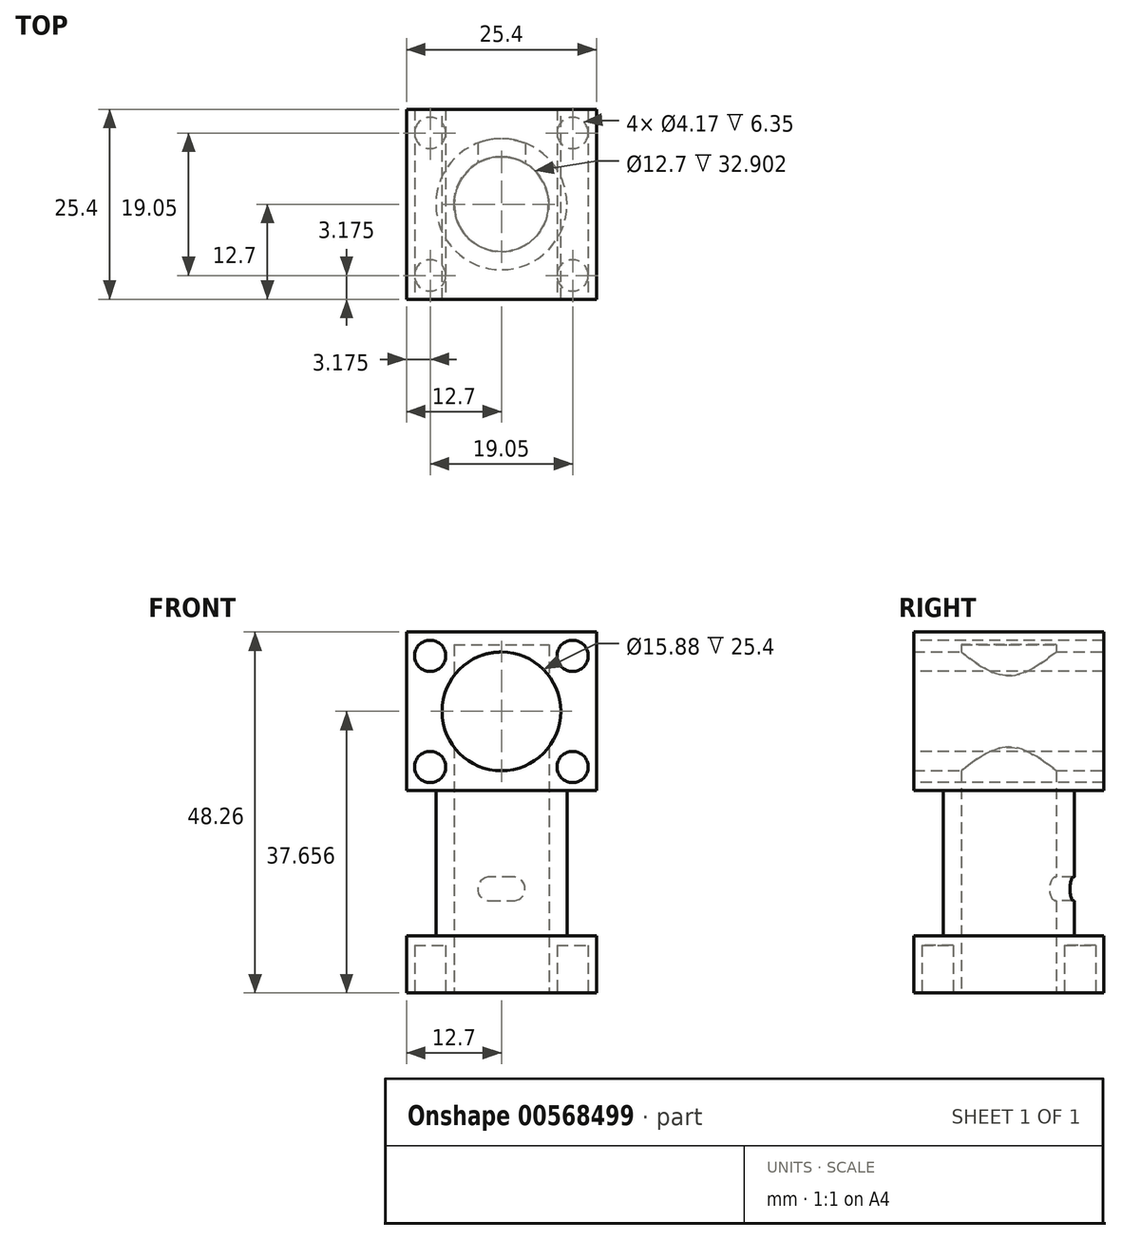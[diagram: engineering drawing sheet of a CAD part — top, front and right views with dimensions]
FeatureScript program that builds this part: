
annotation { "Feature Type Name" : "Feature", "Feature Type Description" : "" }
export const myFeature = defineFeature(function(context is Context, id is Id, definition is map)
    precondition{}
    {
        {
            var Q0;
            Q0=qCreatedBy(makeId("Top.planeOp"),FACE);
            var sketch = newSketch(context, id + "F0", { "sketchPlane" : qUnion([Q0])});
            skLineSegment(sketch, "E0.bottom", {"start": v(12.7, 12.7) * mm, "end": v(-12.7, 12.7) * mm});
            skLineSegment(sketch, "E0.top", {"start": v(12.7, -12.7) * mm, "end": v(-12.7, -12.7) * mm});
            skLineSegment(sketch, "E0.left", {"start": v(12.7, 12.7) * mm, "end": v(12.7, -12.7) * mm});
            skLineSegment(sketch, "E0.right", {"start": v(-12.7, 12.7) * mm, "end": v(-12.7, -12.7) * mm});
            skPoint(sketch, "E0.middle", {"position": v(0, 0) * mm});
            skSolve(sketch);
        }
        {
            var Q0;
            Q0=makeQuery(id+"F0.imprint","IMPRINT",FACE,{"disambiguationData":[TD([[makeQuery(id+"F0.imprint","IMPRINT",EDGE,{"derivedFrom":sQuery(id+"F0.wireOp",EDGE,"E0.bottom")}),1.0]])]});
            extrude(context, id + "F1", {"entities" : qUnion([Q0]), "depth" : 7.62 * mm, "offsetDistance" : 25.4 * mm});
        }
        {
            var Q0;
            Q0=makeQuery(id+"F1.opExtrude","CAP_FACE",FACE,{"disambiguationData":[OSD([sQuery(id+"F0.wireOp",EDGE,"E0.bottom"),sQuery(id+"F0.wireOp",EDGE,"E0.top"),sQuery(id+"F0.wireOp",EDGE,"E0.left"),sQuery(id+"F0.wireOp",EDGE,"E0.right")])],"isStart":false});
            var sketch = newSketch(context, id + "F2", { "sketchPlane" : qUnion([Q0])});
            skCircle(sketch, "E1", {"center": v(0, 0) * mm, "radius": 8.76 * mm});
            skSolve(sketch);
        }
        {
            var Q0;
            Q0 = qSketchRegion(id + "F2", true);
            extrude(context, id + "F3", {"entities" : qUnion([Q0]), "operationType" : NewBodyOperationType.ADD, "depth" : 19.43 * mm, "offsetDistance" : 25.4 * mm});
        }
        {
            var Q0;
            Q0=makeQuery(id+"F3.opExtrude","CAP_FACE",FACE,{"disambiguationData":[OSD([sQuery(id+"F2.wireOp",EDGE,"E1")])],"isStart":false});
            var sketch = newSketch(context, id + "F4", { "sketchPlane" : qUnion([Q0])});
            skLineSegment(sketch, "E2.bottom", {"start": v(12.7, 12.7) * mm, "end": v(-12.7, 12.7) * mm});
            skLineSegment(sketch, "E2.top", {"start": v(12.7, -12.7) * mm, "end": v(-12.7, -12.7) * mm});
            skLineSegment(sketch, "E2.left", {"start": v(12.7, 12.7) * mm, "end": v(12.7, -12.7) * mm});
            skLineSegment(sketch, "E2.right", {"start": v(-12.7, 12.7) * mm, "end": v(-12.7, -12.7) * mm});
            skPoint(sketch, "E2.middle", {"position": v(0, 0) * mm});
            skSolve(sketch);
        }
        {
            var Q0;
            Q0 = qSketchRegion(id + "F4", true);
            extrude(context, id + "F5", {"entities" : qUnion([Q0]), "operationType" : NewBodyOperationType.ADD, "depth" : 21.2 * mm, "offsetDistance" : 25.4 * mm});
        }
        {
            var Q0;
            Q0=makeQuery(id+"F1.opExtrude","CAP_FACE",FACE,{"disambiguationData":[OSD([sQuery(id+"F0.wireOp",EDGE,"E0.bottom"),sQuery(id+"F0.wireOp",EDGE,"E0.top"),sQuery(id+"F0.wireOp",EDGE,"E0.left"),sQuery(id+"F0.wireOp",EDGE,"E0.right")])],"isStart":true});
            var sketch = newSketch(context, id + "F6", { "sketchPlane" : qUnion([Q0])});
            skCircle(sketch, "E3", {"center": v(0, 0) * mm, "radius": 6.35 * mm});
            skSolve(sketch);
        }
        {
            var Q0;
            Q0 = qSketchRegion(id + "F6", true);
            extrude(context, id + "F7", {"entities" : qUnion([Q0]), "operationType" : NewBodyOperationType.REMOVE, "oppositeDirection" : true, "depth" : 46.56 * mm, "offsetDistance" : 25.4 * mm});
        }
        {
            var Q0;
            Q0=makeQuery(id+"F5.opExtrude","SWEPT_FACE",FACE,{"disambiguationData":[OSD([sQuery(id+"F4.wireOp",EDGE,"E2.top")])]});
            var sketch = newSketch(context, id + "F8", { "sketchPlane" : qUnion([Q0])});
            skLineSegment(sketch, "E4", {"start": v(0, 48.26) * mm, "end": v(0, 27.05) * mm});
            skPoint(sketch, "E5", {"position": v(0, 37.66) * mm});
            skCircle(sketch, "E6", {"center": v(0, 37.66) * mm, "radius": 7.94 * mm});
            skCircle(sketch, "E7", {"center": v(-9.53, 45.09) * mm, "radius": 2.08 * mm});
            skCircle(sketch, "E8.1.0.0", {"center": v(9.53, 45.09) * mm, "radius": 2.08 * mm});
            skLineSegment(sketch, "E8.direction1", {"start": v(-9.53, 45.09) * mm, "end": v(9.53, 45.09) * mm, "construction": true});
            skLineSegment(sketch, "E8.direction2", {"start": v(-9.53, 45.09) * mm, "end": v(-9.53, 30.23) * mm, "construction": true});
            skCircle(sketch, "E9.0.0.1", {"center": v(-9.53, 30.23) * mm, "radius": 2.08 * mm});
            skCircle(sketch, "E9.0.1.1", {"center": v(9.53, 30.23) * mm, "radius": 2.08 * mm});
            skSolve(sketch);
        }
        {
            var Q0;
            Q0=makeQuery(id+"F8.imprint","IMPRINT",FACE,{"disambiguationData":[TD([[makeQuery(id+"F8.imprint","IMPRINT",EDGE,{"derivedFrom":sQuery(id+"F8.wireOp",EDGE,"E7")}),1.0]])]});
            var Q1;
            Q1=makeQuery(id+"F8.imprint","IMPRINT",FACE,{"disambiguationData":[TD([[makeQuery(id+"F8.imprint","IMPRINT",EDGE,{"derivedFrom":sQuery(id+"F8.wireOp",EDGE,"E8.1.0.0")}),1.0]])]});
            var Q2;
            Q2=makeQuery(id+"F8.imprint","IMPRINT",FACE,{"disambiguationData":[TD([[makeQuery(id+"F8.imprint","IMPRINT",EDGE,{"derivedFrom":sQuery(id+"F8.wireOp",EDGE,"E9.0.0.1")}),1.0]])]});
            var Q3;
            Q3=makeQuery(id+"F8.imprint","IMPRINT",FACE,{"disambiguationData":[TD([[makeQuery(id+"F8.imprint","IMPRINT",EDGE,{"derivedFrom":sQuery(id+"F8.wireOp",EDGE,"E9.0.1.1")}),1.0]])]});
            extrude(context, id + "F9", {"entities" : qUnion([Q0, Q1, Q2, Q3]), "operationType" : NewBodyOperationType.REMOVE, "endBound" : BoundingType.THROUGH_ALL, "oppositeDirection" : true, "depth" : 6.35 * mm, "offsetDistance" : 25.4 * mm});
        }
        {
            var Q0;
            Q0=makeQuery(id+"F5.opExtrude","SWEPT_FACE",FACE,{"disambiguationData":[OSD([sQuery(id+"F4.wireOp",EDGE,"E2.bottom")])]});
            var sketch = newSketch(context, id + "F10", { "sketchPlane" : qUnion([Q0])});
            skLineSegment(sketch, "E10", {"start": v(0, 48.26) * mm, "end": v(0, 27.05) * mm});
            skCircle(sketch, "E11", {"center": v(0, 37.66) * mm, "radius": 7.94 * mm});
            skSolve(sketch);
        }
        {
            var Q0;
            Q0 = qSketchRegion(id + "F10", true);
            extrude(context, id + "F11", {"entities" : qUnion([Q0]), "operationType" : NewBodyOperationType.REMOVE, "endBound" : BoundingType.THROUGH_ALL, "oppositeDirection" : true, "depth" : 25.4 * mm, "offsetDistance" : 25.4 * mm});
        }
        {
            var Q0;
            Q0=qCreatedBy(makeId("Front.planeOp"),FACE);
            var sketch = newSketch(context, id + "F12", { "sketchPlane" : qUnion([Q0])});
            skLineSegment(sketch, "E12", {"start": v(0, 0) * mm, "end": v(0, 13.92) * mm});
            skLineSegment(sketch, "E13", {"start": v(0, 13.92) * mm, "end": v(1.59, 13.92) * mm});
            skLineSegment(sketch, "E14", {"start": v(0, 13.92) * mm, "end": v(-1.59, 13.92) * mm});
            skCircle(sketch, "E15", {"center": v(1.59, 13.92) * mm, "radius": 1.59 * mm});
            skCircle(sketch, "E16", {"center": v(-1.59, 13.92) * mm, "radius": 1.59 * mm});
            skLineSegment(sketch, "E17", {"start": v(-1.59, 12.33) * mm, "end": v(1.59, 12.33) * mm});
            skLineSegment(sketch, "E18", {"start": v(1.59, 12.33) * mm, "end": v(1.59, 15.5) * mm});
            skLineSegment(sketch, "E19", {"start": v(1.59, 15.5) * mm, "end": v(-1.59, 15.5) * mm});
            skSolve(sketch);
        }
        {
            var Q0;
            Q0 = qSketchRegion(id + "F12", true);
            extrude(context, id + "F13", {"entities" : qUnion([Q0]), "operationType" : NewBodyOperationType.REMOVE, "oppositeDirection" : true, "depth" : 25.4 * mm, "offsetDistance" : 25.4 * mm});
        }
        {
            var Q0;
            Q0=makeQuery(id+"F1.opExtrude","CAP_FACE",FACE,{"disambiguationData":[OSD([sQuery(id+"F0.wireOp",EDGE,"E0.bottom"),sQuery(id+"F0.wireOp",EDGE,"E0.top"),sQuery(id+"F0.wireOp",EDGE,"E0.left"),sQuery(id+"F0.wireOp",EDGE,"E0.right")])],"isStart":true});
            var sketch = newSketch(context, id + "F14", { "sketchPlane" : qUnion([Q0])});
            skCircle(sketch, "E20", {"center": v(-9.53, 9.53) * mm, "radius": 2.08 * mm});
            skCircle(sketch, "E21.0.1.0", {"center": v(-9.53, -9.52) * mm, "radius": 2.08 * mm});
            skCircle(sketch, "E21.1.0.0", {"center": v(9.52, 9.53) * mm, "radius": 2.08 * mm});
            skCircle(sketch, "E21.1.1.0", {"center": v(9.52, -9.52) * mm, "radius": 2.08 * mm});
            skLineSegment(sketch, "E21.direction1", {"start": v(-9.53, 9.53) * mm, "end": v(9.52, 9.53) * mm, "construction": true});
            skLineSegment(sketch, "E21.direction2", {"start": v(-9.53, 9.53) * mm, "end": v(-9.53, -9.52) * mm, "construction": true});
            skSolve(sketch);
        }
        {
            var Q0;
            Q0 = qSketchRegion(id + "F14", true);
            extrude(context, id + "F15", {"entities" : qUnion([Q0]), "operationType" : NewBodyOperationType.REMOVE, "oppositeDirection" : true, "depth" : 6.35 * mm, "offsetDistance" : 25.4 * mm});
        }
    });
